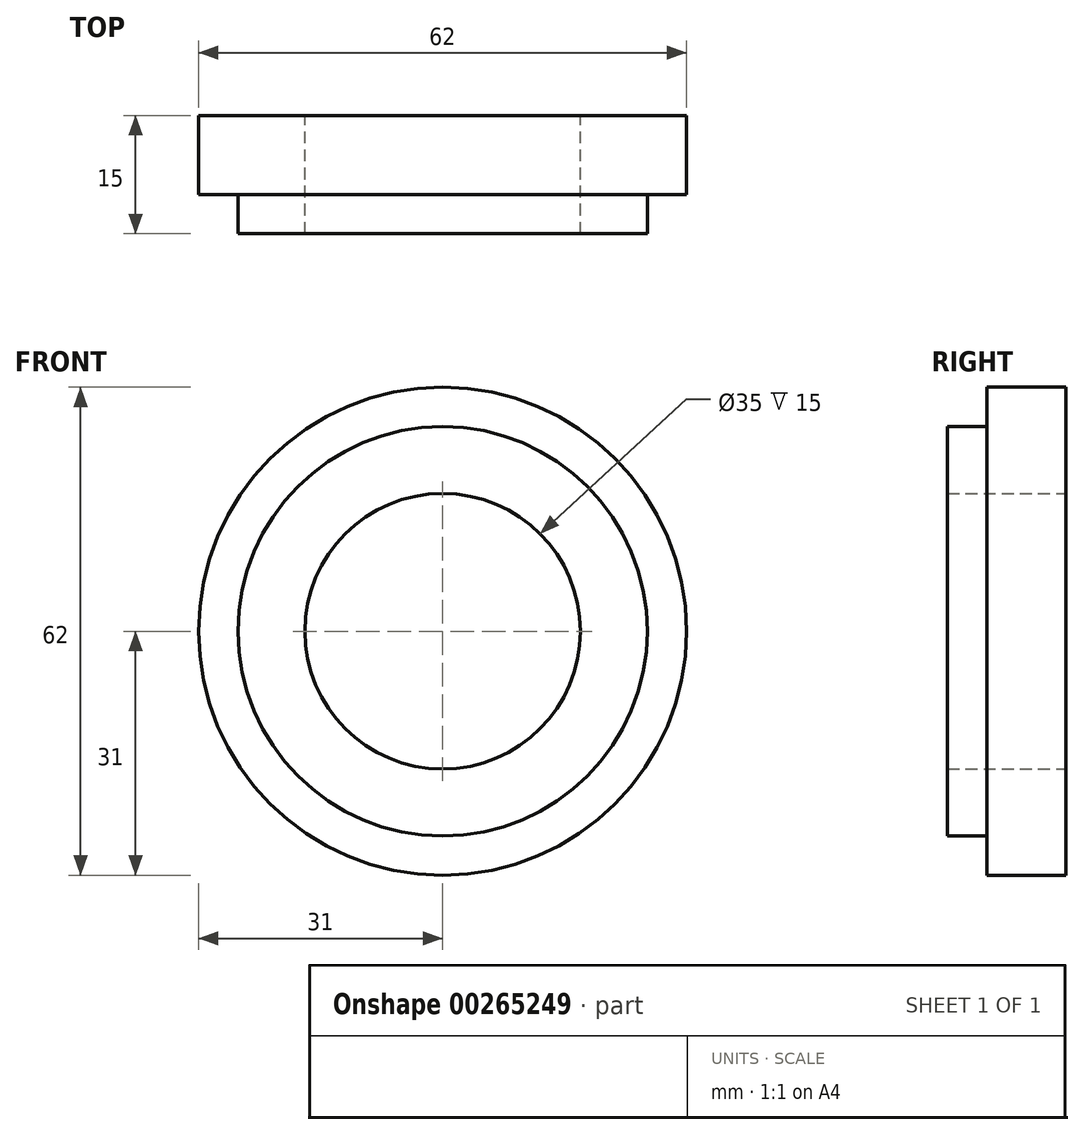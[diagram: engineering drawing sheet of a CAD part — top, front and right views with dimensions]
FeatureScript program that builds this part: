
annotation { "Feature Type Name" : "Feature", "Feature Type Description" : "" }
export const myFeature = defineFeature(function(context is Context, id is Id, definition is map)
    precondition{}
    {
        {
            var Q0;
            Q0=qCreatedBy(makeId("Front.planeOp"),FACE);
            var sketch = newSketch(context, id + "F0", { "sketchPlane" : qUnion([Q0])});
            skCircle(sketch, "E0", {"center": v(0, 0) * mm, "radius": 17.5 * mm});
            skCircle(sketch, "E1", {"center": v(0, 0) * mm, "radius": 31 * mm});
            skSolve(sketch);
        }
        {
            var Q0;
            Q0=makeQuery(id+"F0.imprint","IMPRINT",FACE,{"disambiguationData":[TD([[makeQuery(id+"F0.imprint","IMPRINT",EDGE,{"derivedFrom":sQuery(id+"F0.wireOp",EDGE,"E0")}),-1.0]])]});
            extrude(context, id + "F1", {"entities" : qUnion([Q0]), "depth" : 10 * mm});
        }
        {
            var Q0;
            Q0=makeQuery(id+"F1.opExtrude","CAP_FACE",FACE,{"disambiguationData":[OSD([sQuery(id+"F0.wireOp",EDGE,"E0"),sQuery(id+"F0.wireOp",EDGE,"E1")])],"isStart":false});
            var sketch = newSketch(context, id + "F2", { "sketchPlane" : qUnion([Q0])});
            skCircle(sketch, "E2", {"center": v(0, 0) * mm, "radius": 26 * mm});
            skSolve(sketch);
        }
        {
            var Q0;
            Q0 = qSketchRegion(id + "F2", true);
            extrude(context, id + "F3", {"entities" : qUnion([Q0]), "operationType" : NewBodyOperationType.ADD, "depth" : 5 * mm});
        }
        {
            var Q0;
            Q0=makeQuery(id+"F3.opExtrude","CAP_FACE",FACE,{"disambiguationData":[OSD([sQuery(id+"F2.wireOp",EDGE,"E2")])],"isStart":true});
            extrude(context, id + "F4", {"entities" : qUnion([Q0]), "operationType" : NewBodyOperationType.REMOVE, "oppositeDirection" : true, "depth" : 25.4 * mm});
        }
    });
